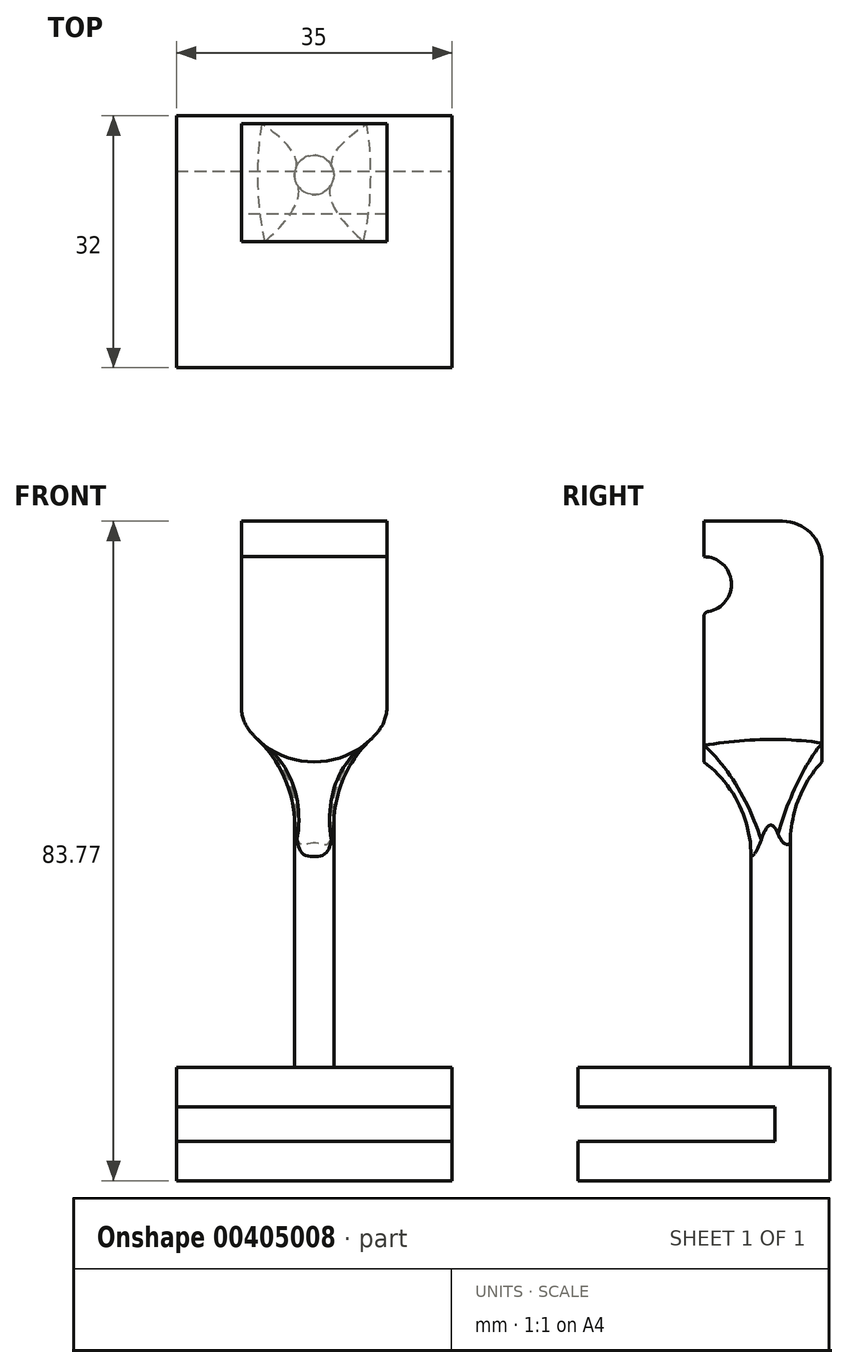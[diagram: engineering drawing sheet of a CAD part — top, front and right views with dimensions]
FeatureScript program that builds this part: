
annotation { "Feature Type Name" : "Feature", "Feature Type Description" : "" }
export const myFeature = defineFeature(function(context is Context, id is Id, definition is map)
    precondition{}
    {
        {
            assignVariable(context, id + "F0", {"name" : "hoogte_staander", "anyValue" : 40});
        }
        {
            assignVariable(context, id + "F1", {"name" : "diepte_plaat", "anyValue" : 25});
        }
        {
            assignVariable(context, id + "F2", {"name" : "dikte_plaat", "anyValue" : 5});
        }
        {
            var Q0;
            Q0=qCreatedBy(makeId("Top.planeOp"),FACE);
            var sketch = newSketch(context, id + "F3", { "sketchPlane" : qUnion([Q0])});
            skLineSegment(sketch, "E0.bottom", {"start": v(17.5, -16) * mm, "end": v(-17.5, -16) * mm});
            skLineSegment(sketch, "E0.top", {"start": v(17.5, 16) * mm, "end": v(-17.5, 16) * mm});
            skLineSegment(sketch, "E0.left", {"start": v(17.5, -16) * mm, "end": v(17.5, 16) * mm});
            skLineSegment(sketch, "E0.right", {"start": v(-17.5, -16) * mm, "end": v(-17.5, 16) * mm});
            skPoint(sketch, "E0.middle", {"position": v(0, 0) * mm});
            skSolve(sketch);
        }
        {
            var Q0;
            Q0 = qSketchRegion(id + "F3", true);
            extrude(context, id + "F4", {"entities" : qUnion([Q0]), "depth" : ((2 * getVariable(context, 'dikte_plaat')) + 4.4) * mm});
        }
        {
            var Q0;
            Q0=makeQuery(id+"F4.opExtrude","SWEPT_FACE",FACE,{"disambiguationData":[OSD([sQuery(id+"F3.wireOp",EDGE,"E0.bottom")])]});
            var sketch = newSketch(context, id + "F5", { "sketchPlane" : qUnion([Q0])});
            skLineSegment(sketch, "E1.bottom", {"start": v(-17.5, 9.4) * mm, "end": v(17.5, 9.4) * mm});
            skLineSegment(sketch, "E1.top", {"start": v(-17.5, 5) * mm, "end": v(17.5, 5) * mm});
            skLineSegment(sketch, "E1.left", {"start": v(-17.5, 9.4) * mm, "end": v(-17.5, 5) * mm});
            skLineSegment(sketch, "E1.right", {"start": v(17.5, 9.4) * mm, "end": v(17.5, 5) * mm});
            skSolve(sketch);
        }
        {
            var Q0;
            Q0 = qSketchRegion(id + "F5", true);
            extrude(context, id + "F6", {"entities" : qUnion([Q0]), "operationType" : NewBodyOperationType.REMOVE, "oppositeDirection" : true, "depth" : (getVariable(context, 'diepte_plaat')) * mm});
        }
        {
            var Q0;
            Q0=makeQuery(id+"F4.opExtrude","CAP_FACE",FACE,{"disambiguationData":[OSD([sQuery(id+"F3.wireOp",EDGE,"E0.bottom"),sQuery(id+"F3.wireOp",EDGE,"E0.top"),sQuery(id+"F3.wireOp",EDGE,"E0.left"),sQuery(id+"F3.wireOp",EDGE,"E0.right")])],"isStart":false});
            var sketch = newSketch(context, id + "F7", { "sketchPlane" : qUnion([Q0])});
            skCircle(sketch, "E2", {"center": v(0, 8.5) * mm, "radius": 2.5 * mm});
            skSolve(sketch);
        }
        {
            var Q0;
            Q0 = qSketchRegion(id + "F7", true);
            extrude(context, id + "F8", {"entities" : qUnion([Q0]), "operationType" : NewBodyOperationType.ADD, "depth" : (getVariable(context, 'hoogte_staander')) * mm});
        }
        {
            var Q0;
            Q0=qCreatedBy(makeId("Front.planeOp"),FACE);
            var sketch = newSketch(context, id + "F9", { "sketchPlane" : qUnion([Q0])});
            skLineSegment(sketch, "E3.bottom", {"start": v(-9.25, 83.77) * mm, "end": v(9.25, 83.77) * mm});
            skLineSegment(sketch, "E3.left", {"start": v(-9.25, 83.77) * mm, "end": v(-9.25, 58.77) * mm});
            skLineSegment(sketch, "E3.right", {"start": v(9.25, 83.77) * mm, "end": v(9.25, 58.77) * mm});
            skArc(sketch, "E4", {"start": v(-9.25, 58.77) * mm, "mid": v(0, 53.2) * mm, "end": v(9.25, 58.77) * mm});
            skSolve(sketch);
        }
        {
            var Q0;
            Q0=makeQuery(id+"F9.imprint","IMPRINT",FACE,{"disambiguationData":[TD([[makeQuery(id+"F9.imprint","IMPRINT",EDGE,{"derivedFrom":sQuery(id+"F9.wireOp",EDGE,"E3.bottom")}),-1.0]])]});
            extrude(context, id + "F10", {"entities" : qUnion([Q0]), "operationType" : NewBodyOperationType.ADD, "oppositeDirection" : true, "depth" : 15 * mm});
        }
        {
            var Q0;
            Q0=makeQuery(id+"F8.opExtrude","CAP_EDGE",EDGE,{"disambiguationData":[OSD([sQuery(id+"F7.wireOp",EDGE,"E2")])],"isStart":true});
            var Q1;
            Q1=makeQuery(id+"F10.boolean.opBoolean","INTERSECT",EDGE,{"derivedFrom":[makeQuery(id+"F8.opExtrude","SWEPT_FACE",FACE,{"disambiguationData":[OSD([sQuery(id+"F7.wireOp",EDGE,"E2")])]}),makeQuery(id+"F10.opExtrude","SWEPT_FACE",FACE,{"disambiguationData":[OSD([sQuery(id+"F9.wireOp",EDGE,"E4")])]})]});
            fillet(context, id + "F11", {"entities" : qUnion([Q0, Q1]), "radius" : 15 * mm, "tangentPropagation" : true, "allowEdgeOverflow" : false});
        }
        {
            var Q0;
            Q0=makeQuery(id+"F10.opExtrude","SWEPT_EDGE",EDGE,{"disambiguationData":[OSD([sQuery(id+"F9.wireOp",EDGE,"E3.right"),sQuery(id+"F9.wireOp",EDGE,"E4")])]});
            var Q1;
            Q1=makeQuery(id+"F10.opExtrude","SWEPT_EDGE",EDGE,{"disambiguationData":[OSD([sQuery(id+"F9.wireOp",EDGE,"E3.left"),sQuery(id+"F9.wireOp",EDGE,"E4")])]});
            fillet(context, id + "F12", {"entities" : qUnion([Q0, Q1]), "radius" : 5 * mm, "tangentPropagation" : true, "allowEdgeOverflow" : false});
        }
        {
            var Q0;
            Q0=makeQuery(id+"F10.opExtrude","SWEPT_FACE",FACE,{"disambiguationData":[OSD([sQuery(id+"F9.wireOp",EDGE,"E3.left")])]});
            var sketch = newSketch(context, id + "F13", { "sketchPlane" : qUnion([Q0])});
            skCircle(sketch, "E5", {"center": v(0, 75.77) * mm, "radius": 3.5 * mm});
            skSolve(sketch);
        }
        {
            var Q0;
            {var subQ0=sQuery(id+"F13.wireOp",EDGE,"E5");var subQ1=makeQuery(id+"F10.opExtrude","CAP_EDGE",EDGE,{"disambiguationData":[OSD([sQuery(id+"F9.wireOp",EDGE,"E3.left")])],"isStart":true});var subQ2=makeQuery(id+"F13.imprint","INTERSECT",VERTEX,{"disambiguationData":[OD(0.0)],"derivedFrom":[subQ1,subQ0]});Q0=makeQuery(id+"F13.imprint","IMPRINT",FACE,{"disambiguationData":[TD([[makeQuery(id+"F13.imprint","IMPRINT",EDGE,{"disambiguationData":[TD([[subQ2,-1.0]])],"derivedFrom":subQ0}),1.0]])]});}
            extrude(context, id + "F14", {"entities" : qUnion([Q0]), "operationType" : NewBodyOperationType.REMOVE, "endBound" : BoundingType.UP_TO_NEXT, "oppositeDirection" : true, "depth" : 25 * mm});
        }
        {
            var Q0;
            {var subQ0=sQuery(id+"F13.wireOp",EDGE,"E5");var subQ1=sQuery(id+"F9.wireOp",EDGE,"E3.left");Q0=makeQuery(id+"F14.boolean.opBoolean","COPY",EDGE,{"derivedFrom":makeQuery(id+"F14.opExtrude","SWEPT_EDGE",EDGE,{"disambiguationData":[OSD([subQ1,subQ0]),TDD([makeQuery(id+"F13.imprint","INTERSECT",VERTEX,{"disambiguationData":[OD(1.0)],"derivedFrom":[makeQuery(id+"F10.opExtrude","CAP_EDGE",EDGE,{"disambiguationData":[OSD([subQ1])],"isStart":true}),subQ0]})])]})});}
            fillet(context, id + "F15", {"entities" : qUnion([Q0]), "radius" : .7 * mm, "tangentPropagation" : true, "allowEdgeOverflow" : false});
        }
        {
            var Q0;
            Q0=makeQuery(id+"F10.opExtrude","CAP_EDGE",EDGE,{"disambiguationData":[OSD([sQuery(id+"F9.wireOp",EDGE,"E3.bottom")])],"isStart":false});
            fillet(context, id + "F16", {"entities" : qUnion([Q0]), "radius" : 5 * mm, "tangentPropagation" : true, "allowEdgeOverflow" : false});
        }
    });
